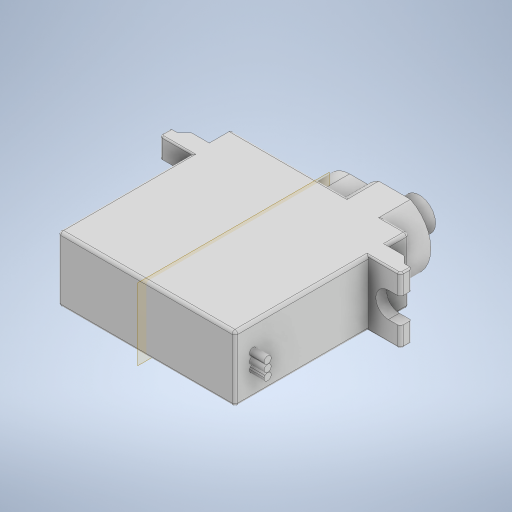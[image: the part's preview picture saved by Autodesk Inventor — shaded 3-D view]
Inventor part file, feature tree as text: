
AUTODESK INVENTOR PART (.ipt)
format: ipt  version: 2023 (Build 270158000, 158)  size: 450,048 bytes
history: native  units: mm
features: extrude x7, sketch x7, projected_geometry x5, fillet x3, other x2, mirror x1
ambient origin geometry x8: Origin, YZ Plane, XZ Plane, XY Plane, X Axis, Y Axis, Z Axis, Center Point
bodies: Body1 (feature_tree)
feature tree (25):
  other  "Bryła1"
  extrude  "Wyciągnięcie proste1"  Depth=24.4mm
  extrude  "Wyciągnięcie proste2"  Depth=24.0mm
  extrude  "Wyciągnięcie proste3"  Depth=9.0mm TaperAngle=0.0deg
  extrude  "Wyciągnięcie proste4"  Depth=18.4mm
  other  "Płaszczyzna konstrukcyjna1"
  mirror  "Odbij1"
  extrude  "Wyciągnięcie proste5"  Depth=1.5mm
  extrude  "Wyciągnięcie proste6"  Depth=2.46mm
  fillet  "Zaokrąglenie1"  Radius=1.5mm
  fillet  "Zaokrąglenie2"  Radius=1.5mm
  fillet  "Zaokrąglenie3"  Radius=4.4mm
  extrude  "Wyciągnięcie proste7"  Depth=1.0mm
  sketch  "Szkic1"
  sketch  "Szkic2"
  projected_geometry  "Pętla rzutowana1"
  sketch  "Szkic3"
  projected_geometry  "Pętla rzutowana2"
  sketch  "Szkic4"
  projected_geometry  "Pętla rzutowana3"
  sketch  "Szkic5"
  projected_geometry  "Pętla rzutowana4"
  sketch  "Szkic6"
  projected_geometry  "Pętla rzutowana5"
  sketch  "Szkic7"
